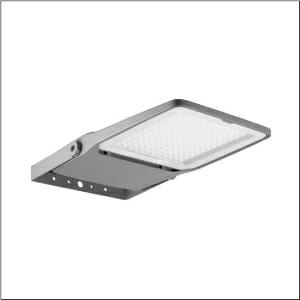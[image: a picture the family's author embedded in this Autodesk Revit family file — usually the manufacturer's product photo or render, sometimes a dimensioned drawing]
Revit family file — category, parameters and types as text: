
# Revit family: floodlight_fl_20_midi___pl61_5xa7682e3c2ac_2046
name_source: partatom
category: Lighting Fixtures
units: mm (PartAtom-declared; Revit-internal decimal feet)

## family parameters
Cut with Voids When Loaded = No
Host = Face
Light Source = No
Part Type = Normal
Room Calculation Point = No
Round Connector Dimension = Use Diameter
Shared = No

## types (1)
- --- (1 x LED 5000K / CRI = 70 (unbekannt), 27570 lm, 5000K)
    Apparent Load = 208 VA
    CIE Flux Codes = 33 65 98 100 100
    Color Rendering = 70
    Color Temperature = 5000K
    Default Elevation = 1800 mm
    Description = Floodlight FL 20 midi, floodlight, primary light control with lens, of plastic, primary optical cover: protective disc, of toughened safety glass, transparent, light distribution: PL61, light emission: direct distribution, primary light characteristic: asymmetric, installation type: surface-mounted, LED, High Power LED, rated luminous flux: 27.570lm, luminous efficacy: 133lm/W, light colour: 750, colour temperature: 5000K, control gear: ECG Plus, control: flexible luminous flux parameterisation, time-dependent luminous flux control, digital communication interface, power reduction, overheat protection, electronic power reduction, with terminal, 5-pole, max. 2.5mm², mains connection: 220..240V, AC, 50/60Hz, rated input power: 208W, LED unit, of diecast aluminium, powder-coated, Siteco® metallic grey (DB 702S), corrosivity category C5 mid according to DIN EN ISO 12944, incl. 1x M20 cable gland for cable Ø 6.5..12mm, length: 731mm, width: 450mm, height: 76mm, housing frame, of diecast aluminium, powder-coated, Siteco® metallic grey (DB 702S), wall fastening, of steel, powder-coated, Siteco® metallic grey (DB 702S), DALI, protection rating (complete): IP66, insulation class (complete): insulation class II (safety insulation), certification: CE, ENEC, VDE, protection symbol: D, permissible operating ambient temperature: -40..+40°C, permissible operating ambient temperature for outdoor applications: -40..+50°C, standard: DIN EN 12944, packaging unit: 1 piece

Light Distribution: PL61
    Height = 76 mm
    Lamp = 1 x LED 5000K / CRI >= 70 (unbekannt)
    Lamp Light Flux = 27570 lm
    Lamp count = 1
    Length = 731 mm
    Luminous efficacy = 133 lm/W
    Manufacturer = Siteco
    ModVariant = No
    Model = 5XA7682E3C2AC
    Mounting Place = Wall
    Mounting Type = Surface mounted
    Number of Poles = 1
    OnlyDefault = Yes
    Power Factor = 1
    Product Name = Floodlight FL 20 midi | PL61
    Product group = floodlight | wall mounted
    ProductGroupID = 2001
    Protection Class = Protection class II
    Protection Degree = IP 66
    RLX_Detail_Level = 1
    RLX_Emergency_Light_Flux = 0 lm
    RLX_Emergency_Type = 0
    RLX_Emergency_Type_DB = No
    RlxData = <blob elided: 92253 chars, md5=1851ea8d>
    Socket = socket
    Standby Power = 0 W
    System Light Flux = 27570 lm
    System Power = 208 W
    Type Comments = factory setting: luminous flux: 100 % | dim-lin: 254 | 484 mA
    Type Image = l_1005944.jpg
    URL = http://relux.com
    VarID = @adj_146809
    Voltage = 0 V
    Weight = 0.00 kg
    Width = 450 mm

## geometry (parser evidence)
native form markers: Blend x4, Sweep x15
no freeform markers — native parametric forms only
